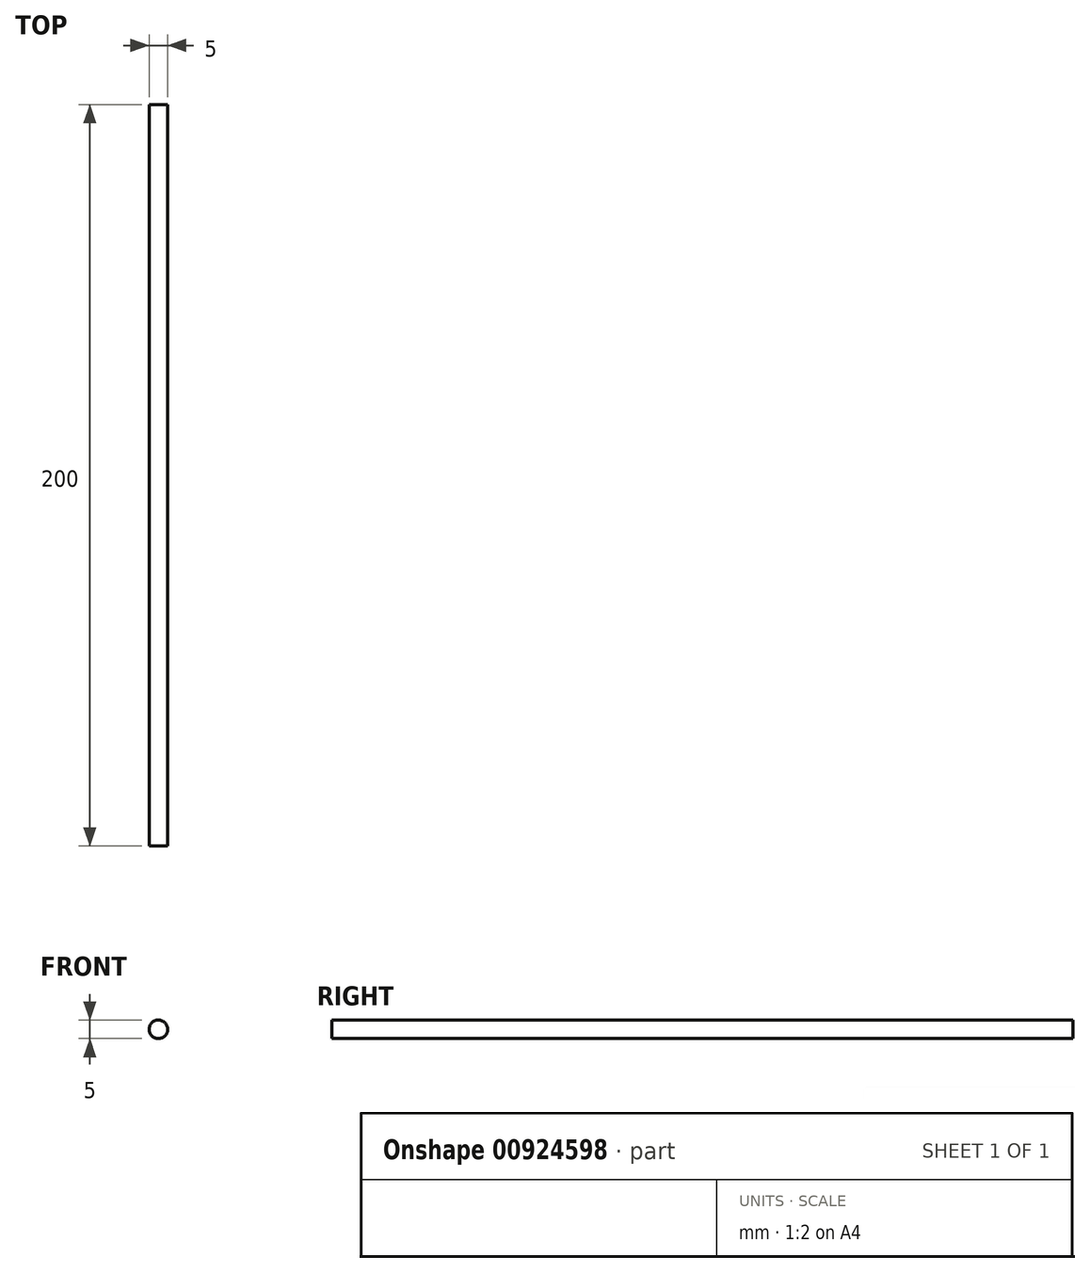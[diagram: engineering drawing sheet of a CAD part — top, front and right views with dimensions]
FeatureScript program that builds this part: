
annotation { "Feature Type Name" : "Feature", "Feature Type Description" : "" }
export const myFeature = defineFeature(function(context is Context, id is Id, definition is map)
    precondition{}
    {
        {
            var Q0;
            Q0=qCreatedBy(makeId("Front.planeOp"),FACE);
            var sketch = newSketch(context, id + "F0", { "sketchPlane" : qUnion([Q0])});
            skCircle(sketch, "E0", {"center": v(0, 0) * mm, "radius": 2.5 * mm});
            skSolve(sketch);
        }
        {
            var Q0;
            Q0=makeQuery(id+"F0.imprint","IMPRINT",FACE,{"disambiguationData":[TD([[makeQuery(id+"F0.imprint","IMPRINT",EDGE,{"derivedFrom":sQuery(id+"F0.wireOp",EDGE,"E0")}),1.0]])]});
            extrude(context, id + "F1", {"entities" : qUnion([Q0]), "depth" : 200 * mm, "offsetDistance" : 25 * mm});
        }
    });
